# Revit family: TermCon_DN15_FF_RFA_2019
name_source: partatom
category: Pipe Accessories
units: mm (PartAtom-declared; Revit-internal decimal feet)

## family parameters
Always vertical = Yes
Cut with Voids When Loaded = No
Part Type = Valve - Breaks Into
Round Connector Dimension = Use Diameter
Shared = No
Work Plane-Based = No

## types (1)
- TemCon DN15 F/F
    CenSd_R3_6 = 12 mm  [stored 0.0393701 ft]
    D = 15 mm
    Description = Automatický termostatický vyvažovací ventil pro rozvody TUV
    H1 = 18 mm  [stored 0.0590551 ft]
    H2 = 4 mm  [stored 0.0131234 ft]
    H3 = 11 mm  [stored 0.0360892 ft]
    H4 = 39 mm
    L1 = 17 mm
    L1__ve = -17 mm
    L2 = 25 mm  [stored 0.082021 ft]
    L2D = 63 mm
    L2D_Min = 30 mm  [stored 0.0984252 ft]
    LT2 = 32 mm
    MC Product Code = 47-2890 DN15 FF (37-65°C, max 100kPa)
    Manufacturer = Hydronic Systems Prague s.r.o.
    QmdConnectorList = 301;D;302;D
    R1 = 15 mm  [stored 0.0492126 ft]
    R2 = 14 mm  [stored 0.0459318 ft]
    R3 = 14 mm  [stored 0.0459318 ft]
    R4 = 15 mm  [stored 0.0492126 ft]
    R5 = 13 mm  [stored 0.0426509 ft]
    R6 = 13 mm  [stored 0.0426509 ft]
    R7 = 12 mm  [stored 0.0393701 ft]
    Type Comments = závitový s vnitřním závitem;  PN10;  max dp=100kPa; pracovní rozsah 10+-100°C; rozsah nastavení 37-65°C; rpzsah nastavení pro bypass 70-80°C;
    URL = www.hydronic.cz
    W = 42 mm  [stored 0.137795 ft]
    W1 = 24 mm  [stored 0.0787402 ft]
    W2D = 15 mm  [stored 0.0492126 ft]
    magiPartTypeId = 306
    magiProductFamilyId = bd44fe9f852841a2a328978ab5ffb8
    magiProductId = b4af831f0cd8469b8a1c3640f49a5f

note: [stored X ft] marks values corroborated as IEEE doubles in the binary element streams (Revit-internal decimal feet)

## geometry (parser evidence)
native form markers: Sweep x2
no freeform markers — native parametric forms only
